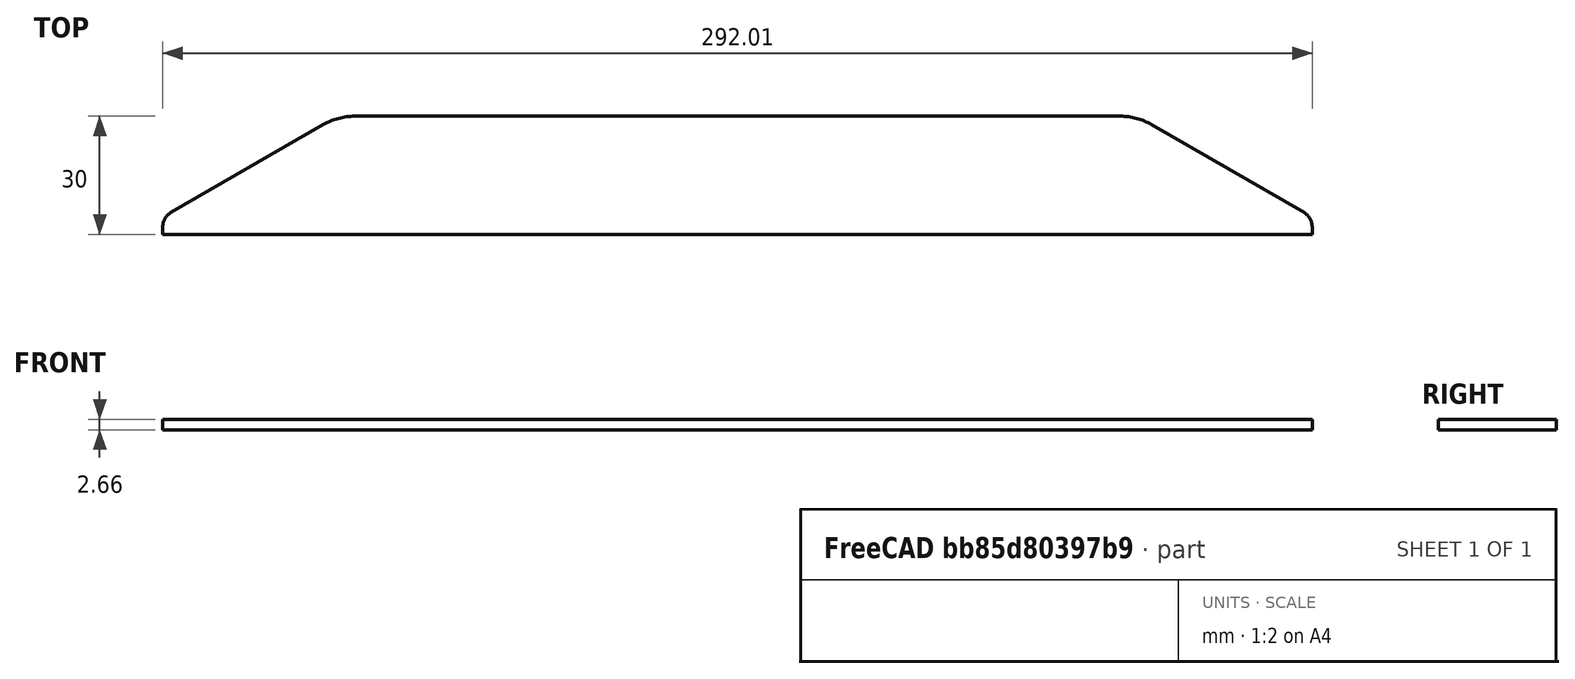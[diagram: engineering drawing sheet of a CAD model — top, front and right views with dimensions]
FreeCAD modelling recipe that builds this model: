
FCSTD DOCUMENT  (FreeCAD 0.20R29177 +426 (Git))
Label: DrivePlatformRib_Path
License: All rights reserved
LicenseURL: http://en.wikipedia.org/wiki/All_rights_reserved
objects: Sketcher::SketchObject×1, PartDesign::Pad×1, PartDesign::Body×1
note: 4 computed .brp shape members not serialized (recipe doc carries the construction recipe); baked Part::Feature solids carry a one-line shape summary decoded from their .brp
EXTERNAL_REF file=DrivePlatform.FCStd obj=Sketch_1
EXTERNAL_REF file=Params.FCStd obj=Spreadsheet

FEATURE [Sketcher::SketchObject] Sketch
  AttachmentOffset = pos=(78.0112,0,0) rot=(1,0,0;1.5708rad)
  FullyConstrained = true
  MapMode = 5
  Placement = pos=(78.0112,0,0) rot=(1,0,0;3.14159rad)
  Support = -> [XZ_Plane001]
  expr: .AttachmentOffset.Base.x = .Constraints.EndOffset
  expr: .Constraints.EndOffset = <<DrivePlatform>>#<<Sketch_1>>.Constraints.BottomOffset
  expr: Constraints[33] = <<Params>>#<<Params>>.TableRollerDriveSupportRadius - 4
  sketch-geometry (14):
    g0: LineSegment StartX=-78.0112 StartY=0 StartZ=0 EndX=214 EndY=0 EndZ=0
    g1: LineSegment StartX=214 StartY=0 StartZ=0 EndX=214 EndY=-2 EndZ=0
    g2: LineSegment StartX=212 StartY=-5.4641 StartZ=0 EndX=173.215 EndY=-27.8564 EndZ=0
    g3: LineSegment StartX=165.215 StartY=-30 StartZ=0 EndX=-29.2266 EndY=-30 EndZ=0
    g4: LineSegment StartX=-37.2266 StartY=-27.8564 StartZ=0 EndX=-76.0112 EndY=-5.4641 EndZ=0
    g5: LineSegment StartX=-78.0112 StartY=-2 StartZ=0 EndX=-78.0112 EndY=0 EndZ=0
    g6: ArcOfCircle CenterX=210 CenterY=-2 CenterZ=0 NormalX=0 NormalY=0 NormalZ=1 AngleXU=0 Radius=4 StartAngle=5.23599 EndAngle=6.28319
    g7: GeomPoint X=214 Y=-4.3094 Z=0
    g8: ArcOfCircle CenterX=-74.0112 CenterY=-2 CenterZ=0 NormalX=0 NormalY=0 NormalZ=1 AngleXU=0 Radius=4 StartAngle=3.14159 EndAngle=4.18879
    g9: GeomPoint X=-78.0112 Y=-4.3094 Z=0
    g10: ArcOfCircle CenterX=-29.2266 CenterY=-14 CenterZ=0 NormalX=0 NormalY=0 NormalZ=1 AngleXU=0 Radius=16 StartAngle=4.18879 EndAngle=4.71239
    g11: GeomPoint X=-33.5137 Y=-30 Z=0
    g12: ArcOfCircle CenterX=165.215 CenterY=-14 CenterZ=0 NormalX=0 NormalY=0 NormalZ=1 AngleXU=0 Radius=16 StartAngle=4.71239 EndAngle=5.23599
    g13: GeomPoint X=169.503 Y=-30 Z=0
  constraints (34):
    c: PointOnObject(g0,g-1)
    c: PointOnObject(g0,g-1)
    c: Coincident(g0,g1)
    c: Vertical(g1)
    c: Horizontal(g3)
    c: Coincident(g5,g0)
    c: Vertical(g5)
    c: PointOnObject(g7,g1)
    c: PointOnObject(g7,g2)
    c: Tangent(g1,g6) = 1.5708
    c: Tangent(g2,g6) = 1.5708
    c: PointOnObject(g9,g4)
    c: PointOnObject(g9,g5)
    c: Tangent(g4,g8) = 1.5708
    c: Tangent(g5,g8) = 1.5708
    c: Equal(g6,g8)
    c: PointOnObject(g11,g3)
    c: PointOnObject(g11,g4)
    c: Tangent(g3,g10) = 1.5708
    c: Tangent(g4,g10) = 1.5708
    c: PointOnObject(g13,g3)
    c: PointOnObject(g13,g2)
    c: Tangent(g3,g12) = 1.5708
    c: Tangent(g2,g12) = 1.5708
    c: Equal(g12,g10)
    c: Radius(g6) = 4
    c: Radius(g12) = 16
    c: Equal(g5,g1)
    c: DistanceY(g1,g1) = 2
    c: DistanceY(g3,g-1) = 30
    c: Angle(g4,g0) = 0.523599
    c: Angle(g0,g2) = 0.523599
    c: DistanceX(g0,g-1) = 78.0112  'EndOffset'
    c: DistanceX(g-1,g0) = 214
FEATURE [PartDesign::Pad] Pad
  Direction = (0,2e-16,-1)
  Length = 2.656
  Length2 = 10
  Midplane = true
  Placement = pos=(0,0,0) rot=(1,0,0;1.5708rad)
  Profile = -> Sketch
  ReferenceAxis = -> Sketch [N_Axis]
  Type = 0
  expr: Length = <<Params>>#<<Params>>.SheetMetalThickness
FEATURE [PartDesign::Body] Body
  Group = -> [Sketch,Pad]
  Origin = -> Origin001
  Tip = -> Pad
